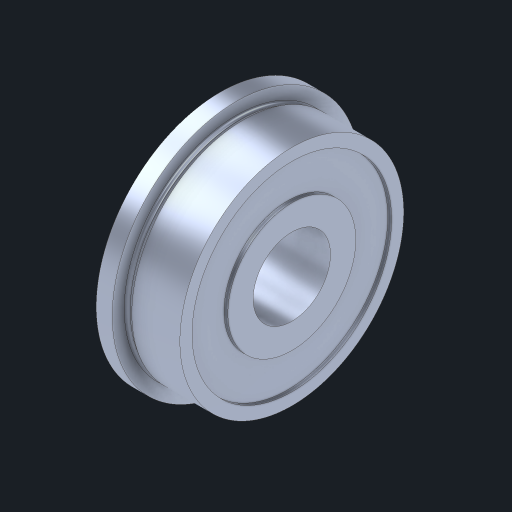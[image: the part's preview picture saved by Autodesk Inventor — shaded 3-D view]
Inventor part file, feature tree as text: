
AUTODESK INVENTOR PART (.ipt)
format: ipt  version: 2023 (Build 270158030, 158C)  size: 210,944 bytes
history: native  units: in
note: dims shown in document units (in); Inventor stores cm internally (conversion verified against a paired STEP export)
features: revolve x1
ambient origin geometry x8: Origin, YZ Plane, XZ Plane, XY Plane, X Axis, Y Axis, Z Axis, Center Point
bodies: Solid1 (feature_tree)
feature tree (1):
  revolve  "Revolve1"  [1 undecoded]
note: 1 required parameter value undecoded (feature->parameter linkage not recoverable at this tier; creation-order binding heuristic only, values carry confidence <= 0.55)
